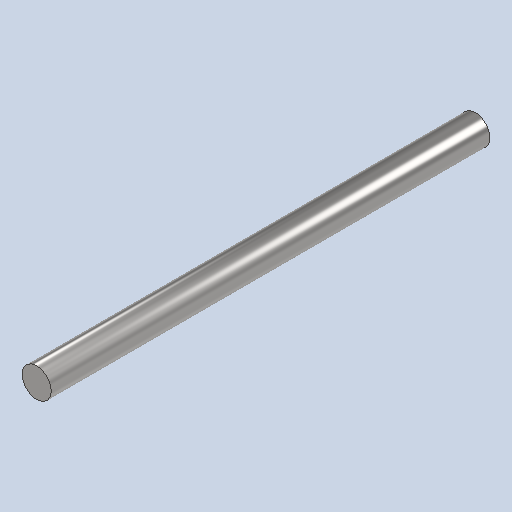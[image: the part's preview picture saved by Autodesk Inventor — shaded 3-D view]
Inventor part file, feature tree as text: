
AUTODESK INVENTOR PART (.ipt)
format: ipt  version: 2023 (Build 270158030, 158C)  size: 258,048 bytes
history: mixed  units: in
note: dims shown in document units (in); Inventor stores cm internally (conversion verified against a paired STEP export)
features: extrude x1, sketch x1, chamfer x1, imported_body x1
ambient origin geometry x8: Origin, YZ Plane, XZ Plane, XY Plane, X Axis, Y Axis, Z Axis, Center Point
bodies: Solid1 (imported_parasolid)
feature tree (4):
  extrude  "Extrusion1"  Depth=0.3937in TaperAngle=0.0deg
  sketch  "Sketch1"  dims[d0=5.9055in d1=0.3937in d2=0.0in]
  chamfer  "Chamfer1"  [1 undecoded]
  imported_body  NMx_Import_Brep_tag  [imported B-rep: ~3 faces, bbox_mm=[0.0, 10.0, 150.0]]
note: 1 required parameter value undecoded (feature->parameter linkage not recoverable at this tier; creation-order binding heuristic only, values carry confidence <= 0.55)
